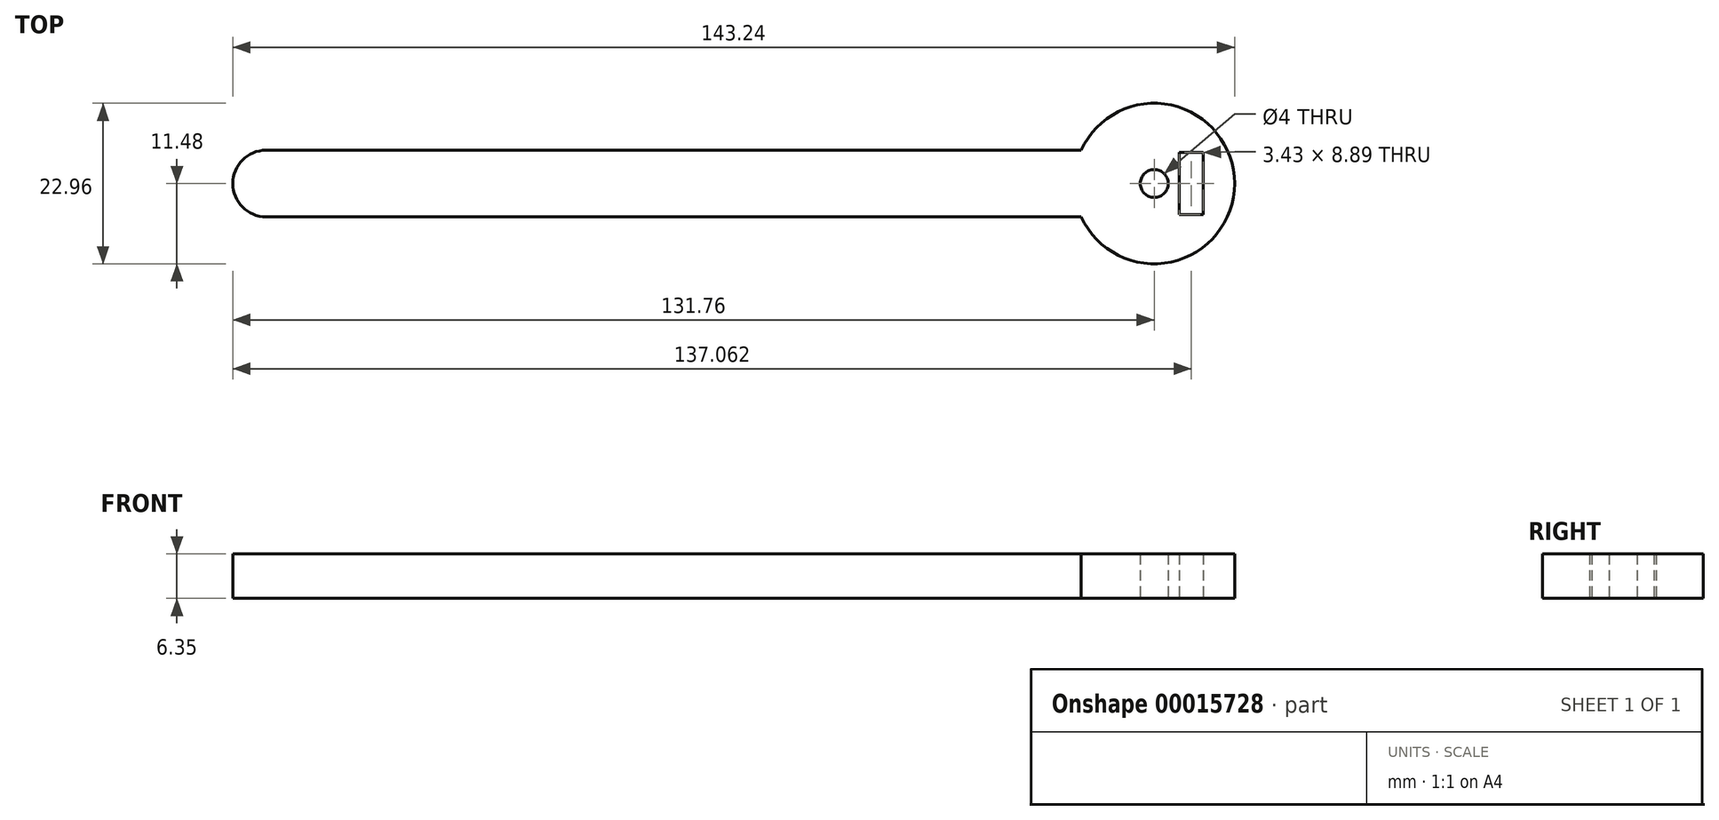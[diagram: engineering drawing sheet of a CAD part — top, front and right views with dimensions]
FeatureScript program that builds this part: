
annotation { "Feature Type Name" : "Feature", "Feature Type Description" : "" }
export const myFeature = defineFeature(function(context is Context, id is Id, definition is map)
    precondition{}
    {
        {
            var Q0;
            Q0=qCreatedBy(makeId("Top.planeOp"),FACE);
            var sketch = newSketch(context, id + "F0", { "sketchPlane" : qUnion([Q0])});
            skArc(sketch, "E0", {"start": v(-10.45, -4.76) * mm, "mid": v(11.48, 0) * mm, "end": v(-10.45, 4.76) * mm});
            skCircle(sketch, "E1", {"center": v(0, 0) * mm, "radius": 2 * mm});
            skLineSegment(sketch, "E2", {"start": v(0, 0) * mm, "end": v(2, 0) * mm, "construction": true});
            skLineSegment(sketch, "E3", {"start": v(2, 0) * mm, "end": v(3.59, 0) * mm, "construction": true});
            skLineSegment(sketch, "E4.bottom", {"start": v(3.59, 4.45) * mm, "end": v(7.02, 4.45) * mm});
            skLineSegment(sketch, "E4.top", {"start": v(3.59, -4.44) * mm, "end": v(7.02, -4.44) * mm});
            skLineSegment(sketch, "E4.left", {"start": v(3.59, 4.45) * mm, "end": v(3.59, -4.45) * mm});
            skLineSegment(sketch, "E4.right", {"start": v(7.02, 4.45) * mm, "end": v(7.02, -4.45) * mm});
            skCircle(sketch, "E5", {"center": v(7.02, -4.44) * mm, "radius": 3.18 * mm, "construction": true});
            skLineSegment(sketch, "E6", {"start": v(0, 0) * mm, "end": v(-10.45, 0) * mm, "construction": true});
            skLineSegment(sketch, "E7.bottom", {"start": v(-10.45, 4.76) * mm, "end": v(-127, 4.76) * mm});
            skLineSegment(sketch, "E7.top", {"start": v(-10.45, -4.76) * mm, "end": v(-127, -4.76) * mm});
            skLineSegment(sketch, "E7.left", {"start": v(-10.45, 4.76) * mm, "end": v(-10.45, -4.76) * mm, "construction": true});
            skLineSegment(sketch, "E7.right", {"start": v(-127, 4.76) * mm, "end": v(-127, -4.76) * mm, "construction": true});
            skArc(sketch, "E8", {"start": v(-127, 4.76) * mm, "mid": v(-131.76, 0) * mm, "end": v(-127, -4.76) * mm});
            skSolve(sketch);
        }
        {
            var Q0;
            Q0 = qSketchRegion(id + "F0", true);
            extrude(context, id + "F1", {"entities" : qUnion([Q0]), "depth" : 6.35 * mm});
        }
    });
